# Revit family: PALADEX_Giunzione_Manicotto
name_source: partatom
category: Accessori per tubazioni
units: mm (PartAtom-declared; Revit-internal decimal feet)

## family parameters
Basato su piano di lavoro = Sì
Condiviso = No
Numero OmniClass = 23.45.00.00
Quota connettore circolare = Usa diametro
Sempre verticale = Sì
Taglio con vuoti quando caricato = Sì
Tipo di parte = Normale
Titolo OmniClass = Sanitary, Laundry, and Cleaning Equipment

## types (23) — shared parameters
Dati = Ta_Mn (15)
Descrizione = PALADEX Tubo Spiralato Composito in Polietilene e Acciaio Zincato
ITA/ENG = No
Immagine tipo = <Nessuno>
Modello = Giunto Manicotto
Produttore = Paladex
URL = www.paladeri.it
URL "Lib bim" = https://bim.paladeri.it
URL Manufacturer = www.paladeri.it
Ver = V15.04
m. = 500 mm
x.[0] = Sì
x.[1] = Sì
x.[4] = Sì
x.[5] = Sì

## per-type parameters (varying)
| type | .a | .b | .c | .d | Bi_L | DIAM | DN | Ma_D | Mn_G | Mo_LN.max | Mo_LN.min | Mo_LT.max | Mo_LT.min | Prospetto di default | Tu_A | x.. |
| ØVar. | 11900 mm | 5950 mm | 12200 mm | 6250 mm | 490 mm | Sì | 400 mm | 438 mm | 400 mm | 11900 mm | 5950 mm | 12200 mm | 6250 mm | 1.219 mm | 440 mm | Sì |
| 02 Ø450 | 11900 mm | 5950 mm | 12200 mm | 6250 mm | 540 mm | Sì | 450 mm | 488 mm | 450 mm | 11900 mm | 5950 mm | 12200 mm | 6250 mm | 0 mm  [stored 0 ft] | 490 mm | Sì |
| 01 Ø400 | 11900 mm | 5950 mm | 12200 mm | 6250 mm | 490 mm | Sì | 400 mm | 438 mm | 400 mm | 11900 mm | 5950 mm | 12200 mm | 6250 mm | 0 mm  [stored 0 ft] | 440 mm | Sì |
| 03 Ø500 | 11900 mm | 5950 mm | 12200 mm | 6250 mm | 590 mm | Sì | 500 mm | 542 mm | 500 mm | 11900 mm | 5950 mm | 12200 mm | 6250 mm | 0 mm  [stored 0 ft] | 540 mm | Sì |
| 04 Ø600 | 11900 mm | 5950 mm | 12200 mm | 6250 mm | 701 mm | Sì | 600 mm | 648 mm | 600 mm | 11900 mm | 5950 mm | 12200 mm | 6250 mm | 0 mm  [stored 0 ft] | 654 mm | Sì |
| 05 Ø700 | 11900 mm | 5950 mm | 12200 mm | 6250 mm | 852 mm | Sì | 700 mm | 772 mm | 700 mm | 11900 mm | 5950 mm | 12200 mm | 6250 mm | 0 mm  [stored 0 ft] | 772 mm | Sì |
| 06 Ø750 | 11900 mm | 5950 mm | 12200 mm | 6250 mm | 884 mm | Sì | 750 mm | 822 mm | 750 mm | 11900 mm | 5950 mm | 12200 mm | 6250 mm | 0 mm  [stored 0 ft] | 822 mm | Sì |
| 07 Ø800 | 13100 mm | 6400 mm | 13400 mm | 6700 mm | 954 mm | Sì | 800 mm | 871 mm | 800 mm | 13100 mm | 6400 mm | 13400 mm | 6700 mm | 0 mm  [stored 0 ft] | 874 mm | Sì |
| 08 Ø900 | 13100 mm | 6400 mm | 13400 mm | 6700 mm | 1034 mm | No | 900 mm | 972 mm | 880 mm | 13100 mm | 6400 mm | 13400 mm | 6700 mm | 0 mm  [stored 0 ft] | 954 mm | No |
| 09 Ø1000 | 13100 mm | 6400 mm | 13400 mm | 6700 mm | 1190 mm | Sì | 1000 mm | 1094 mm | 1000 mm | 13100 mm | 6400 mm | 13400 mm | 6700 mm | 0 mm  [stored 0 ft] | 1090 mm | Sì |
| 10 Ø1100 | 13100 mm | 6400 mm | 13400 mm | 6700 mm | 1290 mm | Sì | 1100 mm | 1190 mm | 1100 mm | 13100 mm | 6400 mm | 13400 mm | 6700 mm | 0 mm  [stored 0 ft] | 1190 mm | Sì |
| 11 Ø1200 | 13100 mm | 6400 mm | 13400 mm | 6700 mm | 1390 mm | Sì | 1200 mm | 1285 mm | 1200 mm | 13100 mm | 6400 mm | 13400 mm | 6700 mm | 0 mm  [stored 0 ft] | 1290 mm | Sì |
| 21 Ø2200 | 11900 mm | 5950 mm | 12200 mm | 6250 mm | 2372 mm | Sì | 2200 mm | 2290 mm | 2200 mm | 11900 mm | 5950 mm | 12200 mm | 6250 mm | 0 mm  [stored 0 ft] | 2290 mm | Sì |
| 20 Ø2100 | 11900 mm | 5950 mm | 12200 mm | 6250 mm | 2272 mm | Sì | 2100 mm | 2190 mm | 2100 mm | 11900 mm | 5950 mm | 12200 mm | 6250 mm | 0 mm  [stored 0 ft] | 2190 mm | Sì |
| 19 Ø2000 | 11900 mm | 5950 mm | 12200 mm | 6250 mm | 2172 mm | Sì | 2000 mm | 2090 mm | 2000 mm | 11900 mm | 5950 mm | 12200 mm | 6250 mm | 0 mm  [stored 0 ft] | 2090 mm | Sì |
| 18 Ø1900 | 11900 mm | 5950 mm | 12200 mm | 6250 mm | 2072 mm | Sì | 1900 mm | 1990 mm | 1900 mm | 11900 mm | 5950 mm | 12200 mm | 6250 mm | 0 mm  [stored 0 ft] | 1990 mm | Sì |
| 17 Ø1800 | 11900 mm | 5950 mm | 12200 mm | 6250 mm | 1972 mm | Sì | 1800 mm | 1890 mm | 1800 mm | 11900 mm | 5950 mm | 12200 mm | 6250 mm | 0 mm  [stored 0 ft] | 1890 mm | Sì |
| 15 Ø1527 | 13100 mm | 6400 mm | 13400 mm | 6700 mm | 1765 mm | Sì | 1527 mm | 1632 mm | 1527 mm | 13100 mm | 6400 mm | 13400 mm | 6700 mm | 0 mm  [stored 0 ft] | 1630 mm | Sì |
| 14 Ø1500 | 13100 mm | 6400 mm | 13400 mm | 6700 mm | 1765 mm | Sì | 1500 mm | 1632 mm | 1500 mm | 13100 mm | 6400 mm | 13400 mm | 6700 mm | 0 mm  [stored 0 ft] | 1625 mm | Sì |
| 13 Ø1400 | 13100 mm | 6400 mm | 13400 mm | 6700 mm | 1630 mm | Sì | 1400 mm | 1530 mm | 1400 mm | 13100 mm | 6400 mm | 13400 mm | 6700 mm | 0 mm  [stored 0 ft] | 1514 mm | Sì |
| 12 Ø1300 | 13100 mm | 6400 mm | 13400 mm | 6700 mm | 1514 mm | Sì | 1300 mm | 1390 mm | 1300 mm | 13100 mm | 6400 mm | 13400 mm | 6700 mm | 0 mm  [stored 0 ft] | 1390 mm | Sì |
| 16 Ø1640 | 13100 mm | 6400 mm | 13400 mm | 6700 mm | 1890 mm | Sì | 1640 mm | 1770 mm | 1640 mm | 13100 mm | 6400 mm | 13400 mm | 6700 mm | 0 mm  [stored 0 ft] | 1765 mm | Sì |
| 99 Øxx | 8000 mm | 4000 mm | 8000 mm | 4000 mm | 420 mm | No | 401 mm | 410 mm | 410 mm | 8000 mm | 4000 mm | 8000 mm | 4000 mm | 0 mm  [stored 0 ft] | 410 mm | No |

note: [stored X ft] marks values corroborated as IEEE doubles in the binary element streams (Revit-internal decimal feet)
